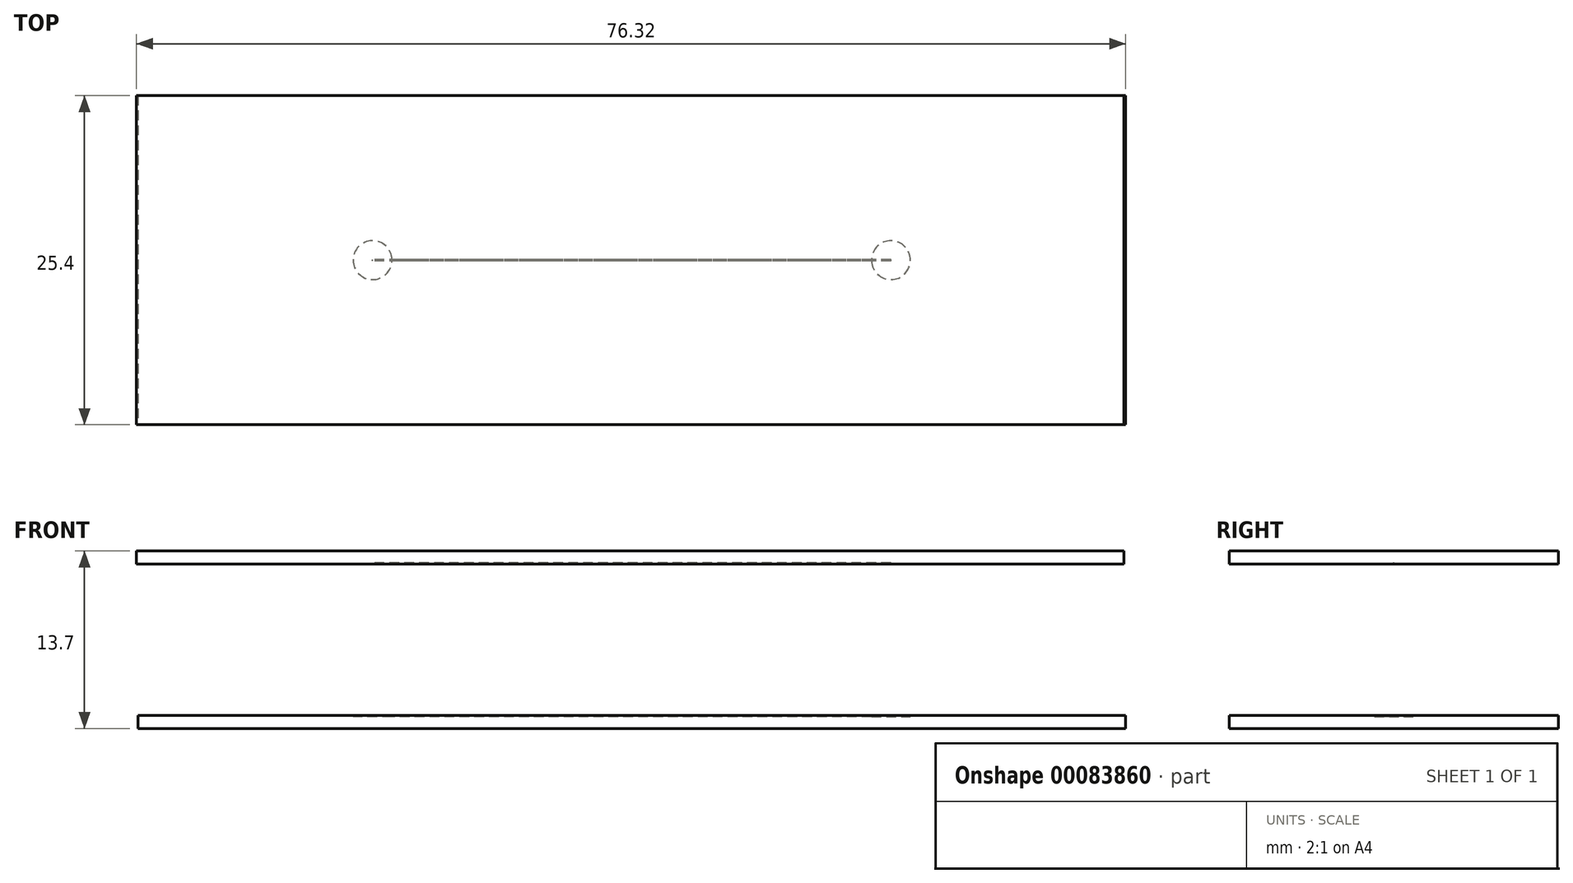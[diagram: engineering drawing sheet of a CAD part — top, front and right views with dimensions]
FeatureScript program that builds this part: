
annotation { "Feature Type Name" : "Feature", "Feature Type Description" : "" }
export const myFeature = defineFeature(function(context is Context, id is Id, definition is map)
    precondition{}
    {
        {
            var Q0;
            Q0=qCreatedBy(makeId("Top.planeOp"),FACE);
            var sketch = newSketch(context, id + "F0", { "sketchPlane" : qUnion([Q0])});
            skLineSegment(sketch, "E0.bottom", {"start": v(38.1, 12.7) * mm, "end": v(-38.1, 12.7) * mm});
            skLineSegment(sketch, "E0.top", {"start": v(38.1, -12.7) * mm, "end": v(-38.1, -12.7) * mm});
            skLineSegment(sketch, "E0.left", {"start": v(38.1, 12.7) * mm, "end": v(38.1, -12.7) * mm});
            skLineSegment(sketch, "E0.right", {"start": v(-38.1, 12.7) * mm, "end": v(-38.1, -12.7) * mm});
            skPoint(sketch, "E0.middle", {"position": v(0, 0) * mm});
            skSolve(sketch);
        }
        {
            var Q0;
            Q0=makeQuery(id+"F0.imprint","IMPRINT",FACE,{"disambiguationData":[TD([[makeQuery(id+"F0.imprint","IMPRINT",EDGE,{"derivedFrom":sQuery(id+"F0.wireOp",EDGE,"E0.bottom")}),1.0]])]});
            extrude(context, id + "F1", {"entities" : qUnion([Q0]), "depth" : 1 * mm});
        }
        {
            var Q0;
            Q0=makeQuery(id+"F1.opExtrude","CAP_FACE",FACE,{"disambiguationData":[OSD([sQuery(id+"F0.wireOp",EDGE,"E0.bottom"),sQuery(id+"F0.wireOp",EDGE,"E0.top"),sQuery(id+"F0.wireOp",EDGE,"E0.left"),sQuery(id+"F0.wireOp",EDGE,"E0.right")])],"isStart":false});
            var sketch = newSketch(context, id + "F2", { "sketchPlane" : qUnion([Q0])});
            skLineSegment(sketch, "E1.bottom", {"start": v(20, 0.05) * mm, "end": v(-20, 0.05) * mm});
            skLineSegment(sketch, "E1.top", {"start": v(20, -0.05) * mm, "end": v(-20, -0.05) * mm});
            skLineSegment(sketch, "E1.left", {"start": v(20, 0.05) * mm, "end": v(20, -0.05) * mm});
            skLineSegment(sketch, "E1.right", {"start": v(-20, 0.05) * mm, "end": v(-20, -0.05) * mm});
            skPoint(sketch, "E1.middle", {"position": v(0, 0) * mm});
            skCircle(sketch, "E2", {"center": v(-20, 0) * mm, "radius": 1.5 * mm});
            skCircle(sketch, "E3", {"center": v(20, 0) * mm, "radius": 1.5 * mm});
            skSolve(sketch);
        }
        {
            var Q0;
            {var subQ0=sQuery(id+"F2.wireOp",EDGE,"E3");var subQ1=sQuery(id+"F2.wireOp",EDGE,"E1.bottom");var subQ2=makeQuery(id+"F2.imprint","INTERSECT",VERTEX,{"derivedFrom":[subQ1,subQ0]});Q0=makeQuery(id+"F2.imprint","IMPRINT",FACE,{"disambiguationData":[TD([[makeQuery(id+"F2.imprint","IMPRINT",EDGE,{"disambiguationData":[TD([[subQ2,-1.0]])],"derivedFrom":subQ1}),1.0]])]});}
            var Q1;
            {var subQ0=sQuery(id+"F2.wireOp",EDGE,"E1.right");Q1=makeQuery(id+"F2.imprint","IMPRINT",FACE,{"disambiguationData":[TD([[makeQuery(id+"F2.imprint","IMPRINT",EDGE,{"derivedFrom":subQ0}),1.0]])]});}
            var Q2;
            {var subQ0=sQuery(id+"F2.wireOp",EDGE,"E1.right");Q2=makeQuery(id+"F2.imprint","IMPRINT",FACE,{"disambiguationData":[TD([[makeQuery(id+"F2.imprint","IMPRINT",EDGE,{"derivedFrom":subQ0}),-1.0]])]});}
            var Q3;
            {var subQ0=sQuery(id+"F2.wireOp",EDGE,"E1.left");Q3=makeQuery(id+"F2.imprint","IMPRINT",FACE,{"disambiguationData":[TD([[makeQuery(id+"F2.imprint","IMPRINT",EDGE,{"derivedFrom":subQ0}),1.0]])]});}
            var Q4;
            {var subQ0=sQuery(id+"F2.wireOp",EDGE,"E1.left");Q4=makeQuery(id+"F2.imprint","IMPRINT",FACE,{"disambiguationData":[TD([[makeQuery(id+"F2.imprint","IMPRINT",EDGE,{"derivedFrom":subQ0}),-1.0]])]});}
            extrude(context, id + "F3", {"entities" : qUnion([Q0, Q1, Q2, Q3, Q4]), "operationType" : NewBodyOperationType.REMOVE, "oppositeDirection" : true, "depth" : 0.1 * mm});
        }
        {
            var Q0;
            Q0=qCreatedBy(makeId("Top.planeOp"),FACE);
            cPlane(context, id + "F4", {"entities" : qUnion([Q0]), "cplaneType" : CPlaneType.OFFSET, "offset" : 12.7 * mm, "width" : 152.4 * mm, "height" : 152.4 * mm});
        }
        {
            var Q0;
            Q0=qCreatedBy(id+"F4.planeOp",FACE);
            var sketch = newSketch(context, id + "F5", { "sketchPlane" : qUnion([Q0])});
            skLineSegment(sketch, "E4.bottom", {"start": v(37.98, 12.7) * mm, "end": v(-38.22, 12.7) * mm});
            skLineSegment(sketch, "E4.top", {"start": v(37.98, -12.7) * mm, "end": v(-38.22, -12.7) * mm});
            skLineSegment(sketch, "E4.left", {"start": v(37.98, 12.7) * mm, "end": v(37.98, -12.7) * mm});
            skLineSegment(sketch, "E4.right", {"start": v(-38.22, 12.7) * mm, "end": v(-38.22, -12.7) * mm});
            skPoint(sketch, "E4.middle", {"position": v(-0.12, 0) * mm});
            skSolve(sketch);
        }
        {
            var Q0;
            Q0=makeQuery(id+"F5.imprint","IMPRINT",FACE,{"disambiguationData":[TD([[makeQuery(id+"F5.imprint","IMPRINT",EDGE,{"derivedFrom":sQuery(id+"F5.wireOp",EDGE,"E4.bottom")}),1.0]])]});
            extrude(context, id + "F6", {"entities" : qUnion([Q0]), "depth" : 1 * mm});
        }
        {
            var Q0;
            Q0=makeQuery(id+"F6.opExtrude","CAP_FACE",FACE,{"disambiguationData":[OSD([sQuery(id+"F5.wireOp",EDGE,"E4.bottom"),sQuery(id+"F5.wireOp",EDGE,"E4.top"),sQuery(id+"F5.wireOp",EDGE,"E4.left"),sQuery(id+"F5.wireOp",EDGE,"E4.right")])],"isStart":true});
            var sketch = newSketch(context, id + "F7", { "sketchPlane" : qUnion([Q0])});
            skLineSegment(sketch, "E5.bottom", {"start": v(20, 0.05) * mm, "end": v(-20, 0.05) * mm});
            skLineSegment(sketch, "E5.top", {"start": v(20, -0.05) * mm, "end": v(-20, -0.05) * mm});
            skLineSegment(sketch, "E5.left", {"start": v(20, 0.05) * mm, "end": v(20, -0.05) * mm});
            skLineSegment(sketch, "E5.right", {"start": v(-20, 0.05) * mm, "end": v(-20, -0.05) * mm});
            skPoint(sketch, "E5.middle", {"position": v(0, 0) * mm});
            skSolve(sketch);
        }
        {
            var Q0;
            Q0=makeQuery(id+"F7.imprint","IMPRINT",FACE,{"disambiguationData":[TD([[makeQuery(id+"F7.imprint","IMPRINT",EDGE,{"derivedFrom":sQuery(id+"F7.wireOp",EDGE,"E5.bottom")}),1.0]])]});
            extrude(context, id + "F8", {"entities" : qUnion([Q0]), "operationType" : NewBodyOperationType.REMOVE, "oppositeDirection" : true, "depth" : 0.1 * mm});
        }
    });
